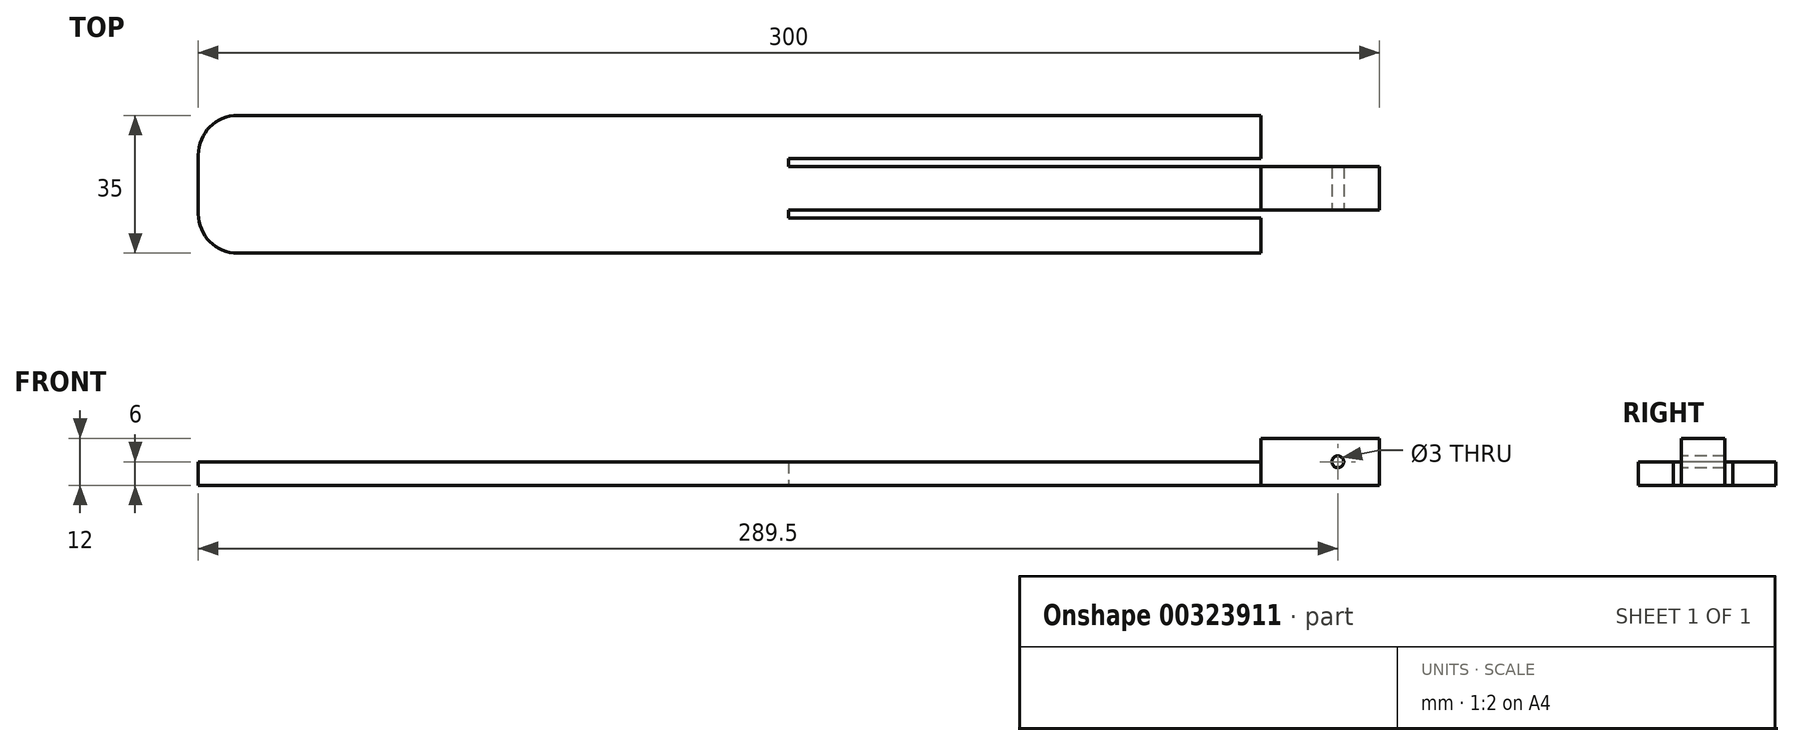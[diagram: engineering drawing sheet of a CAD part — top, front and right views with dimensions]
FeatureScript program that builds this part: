
annotation { "Feature Type Name" : "Feature", "Feature Type Description" : "" }
export const myFeature = defineFeature(function(context is Context, id is Id, definition is map)
    precondition{}
    {
        {
            var Q0;
            Q0=qCreatedBy(makeId("Top.planeOp"),FACE);
            var sketch = newSketch(context, id + "F0", { "sketchPlane" : qUnion([Q0])});
            skLineSegment(sketch, "E0.bottom", {"start": v(-150, 17.5) * mm, "end": v(120, 17.5) * mm});
            skLineSegment(sketch, "E0.top", {"start": v(-150, -17.5) * mm, "end": v(120, -17.5) * mm});
            skLineSegment(sketch, "E0.left", {"start": v(-150, 17.5) * mm, "end": v(-150, -17.5) * mm});
            skPoint(sketch, "E0.middle", {"position": v(0, 0) * mm});
            skLineSegment(sketch, "E1", {"start": v(0, 6.5) * mm, "end": v(120, 6.5) * mm});
            skLineSegment(sketch, "E2", {"start": v(0, 4.5) * mm, "end": v(150, 4.5) * mm});
            skLineSegment(sketch, "E3", {"start": v(0, -8.5) * mm, "end": v(120, -8.5) * mm});
            skLineSegment(sketch, "E4", {"start": v(0, -6.5) * mm, "end": v(150, -6.5) * mm});
            skLineSegment(sketch, "E5", {"start": v(0, -6.5) * mm, "end": v(0, -8.5) * mm});
            skLineSegment(sketch, "E6", {"start": v(0, 6.5) * mm, "end": v(0, 4.5) * mm});
            skLineSegment(sketch, "E7.trimOffspring", {"start": v(150, 4.5) * mm, "end": v(150, -6.5) * mm});
            skLineSegment(sketch, "E8", {"start": v(120, 17.5) * mm, "end": v(120, 6.5) * mm});
            skPoint(sketch, "E0.right.start.orphan", {"position": v(150, 17.5) * mm});
            skPoint(sketch, "E9.trimOffspring.start.orphan", {"position": v(150, -8.5) * mm});
            skPoint(sketch, "E10.orphan", {"position": v(150, -17.5) * mm});
            skLineSegment(sketch, "E11.trimOffspring", {"start": v(120, -8.5) * mm, "end": v(120, -17.5) * mm});
            skSolve(sketch);
        }
        {
            var Q0;
            Q0=makeQuery(id+"F0.imprint","IMPRINT",FACE,{"disambiguationData":[TD([[makeQuery(id+"F0.imprint","IMPRINT",EDGE,{"derivedFrom":sQuery(id+"F0.wireOp",EDGE,"E0.bottom")}),-1.0]])]});
            extrude(context, id + "F1", {"entities" : qUnion([Q0]), "depth" : 6 * mm});
        }
        {
            var Q0;
            Q0=makeQuery(id+"F1.opExtrude","SWEPT_EDGE",EDGE,{"disambiguationData":[OSD([sQuery(id+"F0.wireOp",EDGE,"E0.top"),sQuery(id+"F0.wireOp",EDGE,"E0.left")])]});
            var Q1;
            Q1=makeQuery(id+"F1.opExtrude","SWEPT_EDGE",EDGE,{"disambiguationData":[OSD([sQuery(id+"F0.wireOp",EDGE,"E0.bottom"),sQuery(id+"F0.wireOp",EDGE,"E0.left")])]});
            fillet(context, id + "F2", {"entities" : qUnion([Q0, Q1]), "radius" : 10 * mm, "tangentPropagation" : true, "allowEdgeOverflow" : false});
        }
        {
            var Q0;
            Q0=makeQuery(id+"F1.opExtrude","CAP_FACE",FACE,{"disambiguationData":[OSD([sQuery(id+"F0.wireOp",EDGE,"E0.bottom"),sQuery(id+"F0.wireOp",EDGE,"E0.top"),sQuery(id+"F0.wireOp",EDGE,"E0.left"),sQuery(id+"F0.wireOp",EDGE,"E1"),sQuery(id+"F0.wireOp",EDGE,"E2"),sQuery(id+"F0.wireOp",EDGE,"E3"),sQuery(id+"F0.wireOp",EDGE,"E4"),sQuery(id+"F0.wireOp",EDGE,"E5"),sQuery(id+"F0.wireOp",EDGE,"E6"),sQuery(id+"F0.wireOp",EDGE,"E7.trimOffspring"),sQuery(id+"F0.wireOp",EDGE,"E8"),sQuery(id+"F0.wireOp",EDGE,"E11.trimOffspring")])],"isStart":false});
            var sketch = newSketch(context, id + "F3", { "sketchPlane" : qUnion([Q0])});
            skLineSegment(sketch, "E12.bottom", {"start": v(120, 4.5) * mm, "end": v(150, 4.5) * mm});
            skLineSegment(sketch, "E12.top", {"start": v(120, -6.5) * mm, "end": v(150, -6.5) * mm});
            skLineSegment(sketch, "E12.left", {"start": v(120, 4.5) * mm, "end": v(120, -6.5) * mm});
            skLineSegment(sketch, "E12.right", {"start": v(150, 4.5) * mm, "end": v(150, -6.5) * mm});
            skSolve(sketch);
        }
        {
            var Q0;
            Q0=makeQuery(id+"F3.imprint","IMPRINT",FACE,{"disambiguationData":[TD([[makeQuery(id+"F3.imprint","IMPRINT",EDGE,{"derivedFrom":sQuery(id+"F3.wireOp",EDGE,"E12.bottom")}),-1.0]])]});
            extrude(context, id + "F4", {"entities" : qUnion([Q0]), "operationType" : NewBodyOperationType.ADD, "depth" : 6 * mm});
        }
        {
            var Q0;
            Q0=makeQuery(id+"F4.boolean.opBoolean","MERGE",FACE,{"derivedFrom":[makeQuery(id+"F1.opExtrude","SWEPT_FACE",FACE,{"disambiguationData":[OSD([sQuery(id+"F0.wireOp",EDGE,"E4")])]}),makeQuery(id+"F4.opExtrude","SWEPT_FACE",FACE,{"disambiguationData":[OSD([sQuery(id+"F3.wireOp",EDGE,"E12.top")])]})]});
            var sketch = newSketch(context, id + "F5", { "sketchPlane" : qUnion([Q0])});
            skCircle(sketch, "E13", {"center": v(139.5, 6) * mm, "radius": 1.5 * mm});
            skPoint(sketch, "E13.centerSnap0", {"position": v(150, 6) * mm});
            skSolve(sketch);
        }
        {
            var Q0;
            Q0=makeQuery(id+"F5.imprint","IMPRINT",FACE,{"disambiguationData":[TD([[makeQuery(id+"F5.imprint","IMPRINT",EDGE,{"derivedFrom":sQuery(id+"F5.wireOp",EDGE,"E13")}),1.0]])]});
            extrude(context, id + "F6", {"entities" : qUnion([Q0]), "operationType" : NewBodyOperationType.REMOVE, "oppositeDirection" : true, "depth" : 25 * mm});
        }
    });
